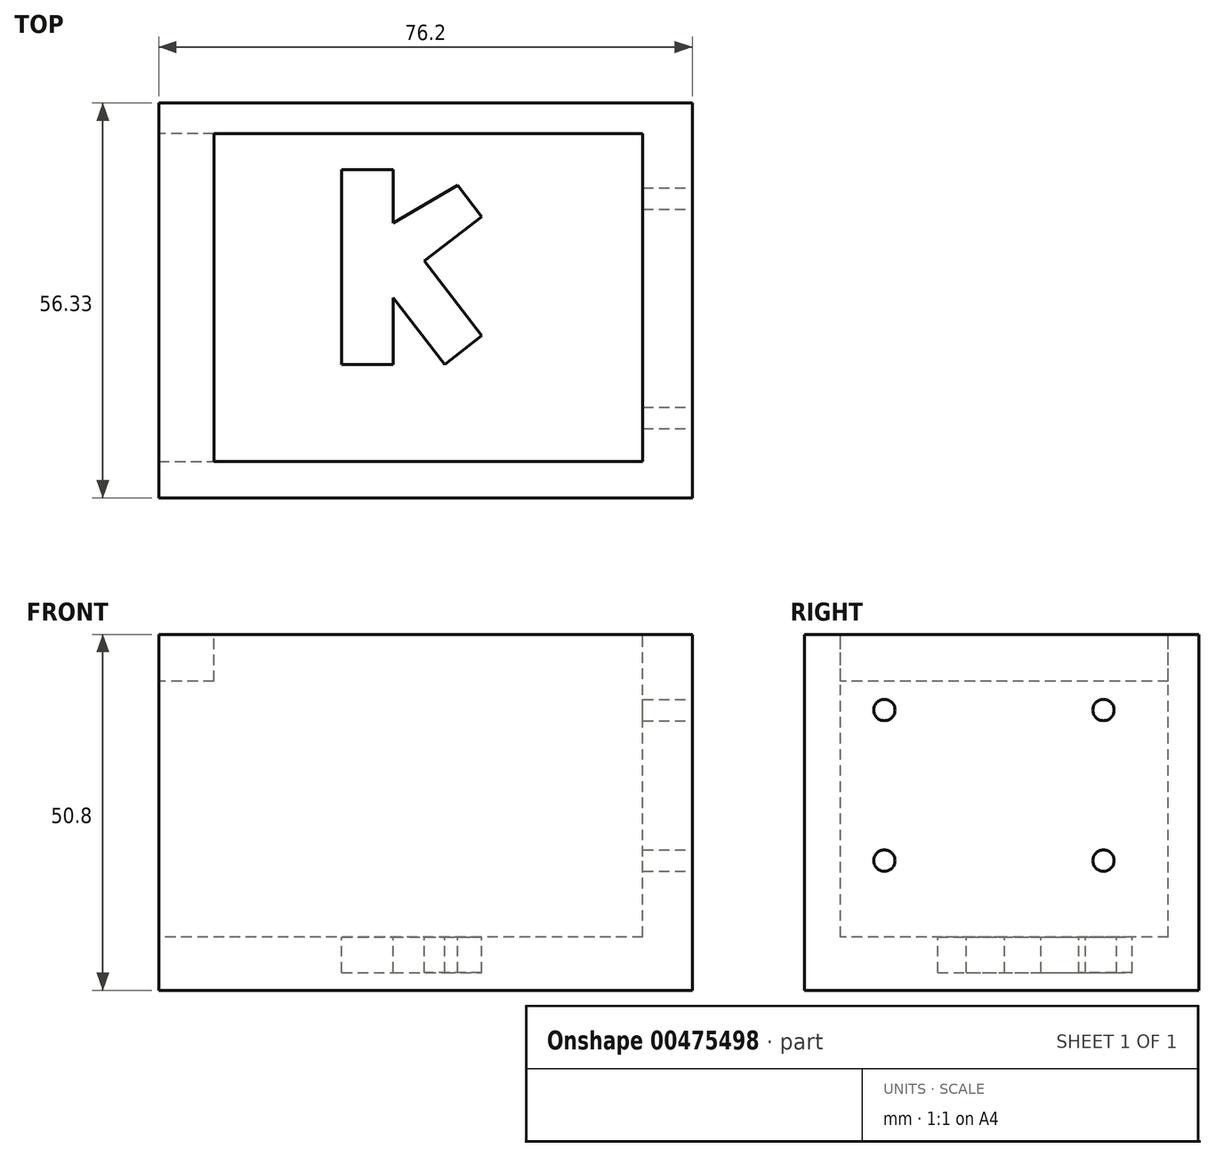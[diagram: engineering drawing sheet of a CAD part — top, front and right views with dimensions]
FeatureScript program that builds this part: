
annotation { "Feature Type Name" : "Feature", "Feature Type Description" : "" }
export const myFeature = defineFeature(function(context is Context, id is Id, definition is map)
    precondition{}
    {
        {
            var Q0;
            Q0=qCreatedBy(makeId("Top.planeOp"),FACE);
            var sketch = newSketch(context, id + "F0", { "sketchPlane" : qUnion([Q0])});
            skLineSegment(sketch, "E0.bottom", {"start": v(0, 0) * mm, "end": v(76.2, 0) * mm});
            skLineSegment(sketch, "E0.top", {"start": v(0, -56.33) * mm, "end": v(76.2, -56.33) * mm});
            skLineSegment(sketch, "E0.left", {"start": v(0, 0) * mm, "end": v(0, -56.33) * mm});
            skLineSegment(sketch, "E0.right", {"start": v(76.2, 0) * mm, "end": v(76.2, -56.33) * mm});
            skSolve(sketch);
        }
        {
            var Q0;
            Q0=makeQuery(id+"F0.imprint","IMPRINT",FACE,{"disambiguationData":[TD([[makeQuery(id+"F0.imprint","IMPRINT",EDGE,{"derivedFrom":sQuery(id+"F0.wireOp",EDGE,"E0.bottom")}),-1.0]])]});
            extrude(context, id + "F1", {"entities" : qUnion([Q0]), "depth" : 50.8 * mm});
        }
        {
            var Q0;
            Q0=makeQuery(id+"F1.opExtrude","CAP_FACE",FACE,{"disambiguationData":[OSD([sQuery(id+"F0.wireOp",EDGE,"E0.bottom"),sQuery(id+"F0.wireOp",EDGE,"E0.top"),sQuery(id+"F0.wireOp",EDGE,"E0.left"),sQuery(id+"F0.wireOp",EDGE,"E0.right")])],"isStart":false});
            var sketch = newSketch(context, id + "F2", { "sketchPlane" : qUnion([Q0])});
            skLineSegment(sketch, "E1", {"start": v(7.9, -4.35) * mm, "end": v(7.9, -51.16) * mm});
            skLineSegment(sketch, "E2", {"start": v(7.9, -51.16) * mm, "end": v(69.12, -51.16) * mm});
            skLineSegment(sketch, "E3", {"start": v(69.12, -51.16) * mm, "end": v(69.12, -4.35) * mm});
            skLineSegment(sketch, "E4", {"start": v(69.12, -4.35) * mm, "end": v(7.9, -4.35) * mm});
            skSolve(sketch);
        }
        {
            var Q0;
            Q0=makeQuery(id+"F2.imprint","IMPRINT",FACE,{"disambiguationData":[TD([[makeQuery(id+"F2.imprint","IMPRINT",EDGE,{"derivedFrom":sQuery(id+"F2.wireOp",EDGE,"E1")}),1.0]])]});
            extrude(context, id + "F3", {"entities" : qUnion([Q0]), "operationType" : NewBodyOperationType.REMOVE, "oppositeDirection" : true, "depth" : 43.18 * mm});
        }
        {
            var Q0;
            Q0=makeQuery(id+"F3.boolean.opBoolean","COPY",FACE,{"derivedFrom":makeQuery(id+"F3.opExtrude","SWEPT_FACE",FACE,{"disambiguationData":[OSD([sQuery(id+"F2.wireOp",EDGE,"E1")])]})});
            var sketch = newSketch(context, id + "F4", { "sketchPlane" : qUnion([Q0])});
            skLineSegment(sketch, "E5", {"start": v(-51.16, 7.62) * mm, "end": v(-4.35, 7.62) * mm});
            skLineSegment(sketch, "E6", {"start": v(-4.35, 7.62) * mm, "end": v(-4.35, 29.21) * mm});
            skLineSegment(sketch, "E7", {"start": v(-4.35, 29.21) * mm, "end": v(-51.16, 29.21) * mm});
            skLineSegment(sketch, "E8", {"start": v(-51.16, 29.21) * mm, "end": v(-51.16, 7.62) * mm});
            skSolve(sketch);
        }
        {
            var Q0;
            Q0 = qSketchRegion(id + "F4", true);
            extrude(context, id + "F5", {"entities" : qUnion([Q0]), "operationType" : NewBodyOperationType.REMOVE, "oppositeDirection" : true, "depth" : 25.4 * mm});
        }
        {
            var Q0;
            Q0=makeQuery(id+"F1.opExtrude","SWEPT_FACE",FACE,{"disambiguationData":[OSD([sQuery(id+"F0.wireOp",EDGE,"E0.left")])]});
            var sketch = newSketch(context, id + "F6", { "sketchPlane" : qUnion([Q0])});
            skLineSegment(sketch, "E9", {"start": v(4.35, 29.21) * mm, "end": v(4.35, 38.44) * mm});
            skLineSegment(sketch, "E10", {"start": v(4.35, 38.44) * mm, "end": v(51.16, 38.44) * mm});
            skLineSegment(sketch, "E11", {"start": v(51.16, 38.44) * mm, "end": v(51.16, 29.21) * mm});
            skSolve(sketch);
        }
        {
            var Q0;
            Q0=makeQuery(id+"F6.imprint","IMPRINT",FACE,{"disambiguationData":[TD([[makeQuery(id+"F6.imprint","IMPRINT",EDGE,{"derivedFrom":sQuery(id+"F6.wireOp",EDGE,"E9")}),-1.0]])]});
            extrude(context, id + "F7", {"entities" : qUnion([Q0]), "operationType" : NewBodyOperationType.REMOVE, "oppositeDirection" : true, "depth" : 25.4 * mm});
        }
        {
            var Q0;
            Q0=makeQuery(id+"F5.boolean.opBoolean","MERGE",FACE,{"derivedFrom":[makeQuery(id+"F3.boolean.opBoolean","COPY",FACE,{"derivedFrom":makeQuery(id+"F3.opExtrude","CAP_FACE",FACE,{"disambiguationData":[OSD([sQuery(id+"F2.wireOp",EDGE,"E1"),sQuery(id+"F2.wireOp",EDGE,"E2"),sQuery(id+"F2.wireOp",EDGE,"E3"),sQuery(id+"F2.wireOp",EDGE,"E4")])],"isStart":false})}),makeQuery(id+"F5.opExtrude","SWEPT_FACE",FACE,{"disambiguationData":[OSD([sQuery(id+"F4.wireOp",EDGE,"E5")])]})]});
            var sketch = newSketch(context, id + "F8", { "sketchPlane" : qUnion([Q0])});
            skLineSegment(sketch, "E12", {"start": v(26.13, -16.6) * mm, "end": v(26.13, -37.28) * mm});
            skLineSegment(sketch, "E13", {"start": v(26.13, -37.28) * mm, "end": v(33.47, -37.28) * mm});
            skLineSegment(sketch, "E14", {"start": v(33.47, -37.28) * mm, "end": v(33.47, -27.76) * mm});
            skLineSegment(sketch, "E15", {"start": v(33.47, -27.76) * mm, "end": v(40.82, -37.28) * mm});
            skLineSegment(sketch, "E16", {"start": v(40.82, -37.28) * mm, "end": v(46.13, -33.19) * mm});
            skLineSegment(sketch, "E17", {"start": v(46.13, -33.19) * mm, "end": v(37.91, -22.54) * mm});
            skLineSegment(sketch, "E18", {"start": v(37.91, -22.54) * mm, "end": v(46.13, -16.2) * mm});
            skLineSegment(sketch, "E19", {"start": v(46.13, -16.2) * mm, "end": v(42.66, -11.7) * mm});
            skLineSegment(sketch, "E20", {"start": v(26.13, -16.6) * mm, "end": v(26.13, -9.53) * mm});
            skLineSegment(sketch, "E21", {"start": v(26.13, -9.53) * mm, "end": v(33.47, -9.53) * mm});
            skLineSegment(sketch, "E22", {"start": v(33.47, -9.53) * mm, "end": v(33.47, -17.1) * mm});
            skLineSegment(sketch, "E23", {"start": v(33.47, -17.1) * mm, "end": v(42.66, -11.7) * mm});
            skSolve(sketch);
        }
        {
            var Q0;
            Q0=makeQuery(id+"F8.imprint","IMPRINT",FACE,{"disambiguationData":[TD([[makeQuery(id+"F8.imprint","IMPRINT",EDGE,{"derivedFrom":sQuery(id+"F8.wireOp",EDGE,"E12")}),1.0]])]});
            extrude(context, id + "F9", {"entities" : qUnion([Q0]), "operationType" : NewBodyOperationType.REMOVE, "oppositeDirection" : true, "depth" : 5.08 * mm});
        }
        {
            var Q0;
            Q0=makeQuery(id+"F1.opExtrude","SWEPT_FACE",FACE,{"disambiguationData":[OSD([sQuery(id+"F0.wireOp",EDGE,"E0.right")])]});
            var sketch = newSketch(context, id + "F10", { "sketchPlane" : qUnion([Q0])});
            skCircle(sketch, "E24", {"center": v(-44.9, 40) * mm, "radius": 1.52 * mm});
            skCircle(sketch, "E25", {"center": v(-13.6, 40) * mm, "radius": 1.52 * mm});
            skCircle(sketch, "E26", {"center": v(-44.9, 18.5) * mm, "radius": 1.52 * mm});
            skCircle(sketch, "E27", {"center": v(-13.6, 18.5) * mm, "radius": 1.52 * mm});
            skSolve(sketch);
        }
        {
            var Q0;
            Q0=makeQuery(id+"F10.imprint","IMPRINT",FACE,{"disambiguationData":[TD([[makeQuery(id+"F10.imprint","IMPRINT",EDGE,{"derivedFrom":sQuery(id+"F10.wireOp",EDGE,"E26")}),1.0]])]});
            var Q1;
            Q1=makeQuery(id+"F10.imprint","IMPRINT",FACE,{"disambiguationData":[TD([[makeQuery(id+"F10.imprint","IMPRINT",EDGE,{"derivedFrom":sQuery(id+"F10.wireOp",EDGE,"E25")}),1.0]])]});
            var Q2;
            Q2=makeQuery(id+"F10.imprint","IMPRINT",FACE,{"disambiguationData":[TD([[makeQuery(id+"F10.imprint","IMPRINT",EDGE,{"derivedFrom":sQuery(id+"F10.wireOp",EDGE,"E24")}),1.0]])]});
            var Q3;
            Q3=makeQuery(id+"F10.imprint","IMPRINT",FACE,{"disambiguationData":[TD([[makeQuery(id+"F10.imprint","IMPRINT",EDGE,{"derivedFrom":sQuery(id+"F10.wireOp",EDGE,"E27")}),1.0]])]});
            extrude(context, id + "F11", {"entities" : qUnion([Q0, Q1, Q2, Q3]), "operationType" : NewBodyOperationType.REMOVE, "oppositeDirection" : true, "depth" : 25.4 * mm});
        }
        {
            var Q0;
            Q0=makeQuery(id+"F1.opExtrude","SWEPT_FACE",FACE,{"disambiguationData":[OSD([sQuery(id+"F0.wireOp",EDGE,"E0.left")])]});
            var sketch = newSketch(context, id + "F12", { "sketchPlane" : qUnion([Q0])});
            skLineSegment(sketch, "E28", {"start": v(4.35, 38.44) * mm, "end": v(4.35, 44.1) * mm});
            skLineSegment(sketch, "E29", {"start": v(4.35, 44.1) * mm, "end": v(51.16, 44.1) * mm});
            skLineSegment(sketch, "E30", {"start": v(51.16, 44.1) * mm, "end": v(51.16, 38.44) * mm});
            skLineSegment(sketch, "E31", {"start": v(51.16, 38.44) * mm, "end": v(4.35, 38.44) * mm});
            skSolve(sketch);
        }
        {
            var Q0;
            Q0=makeQuery(id+"F12.imprint","IMPRINT",FACE,{"disambiguationData":[TD([[makeQuery(id+"F12.imprint","IMPRINT",EDGE,{"derivedFrom":sQuery(id+"F12.wireOp",EDGE,"E28")}),-1.0]])]});
            extrude(context, id + "F13", {"entities" : qUnion([Q0]), "operationType" : NewBodyOperationType.REMOVE, "oppositeDirection" : true, "depth" : 25.4 * mm});
        }
    });
